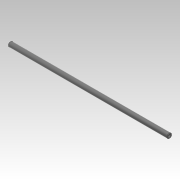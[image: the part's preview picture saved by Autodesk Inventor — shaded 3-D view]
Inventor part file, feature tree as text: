
AUTODESK INVENTOR PART (.ipt)
format: ipt  version: 2020 (Build 240168000, 168)  size: 91,136 bytes
history: native  units: mm
features: revolve x1, chamfer x1, sketch x1
ambient origin geometry x8: Origin, YZ Plane, XZ Plane, XY Plane, X Axis, Y Axis, Z Axis, Center Point
bodies: Solid1 (feature_tree)
feature tree (3):
  revolve  "Revolution1"  [1 undecoded]
  chamfer  "Chamfer1"  Distance=200.0mm
  sketch  "Sketch1"  dims[d0=2.0mm d1=3.0mm d2=200.0mm d3=90.0deg d4=0.5mm d5=2.0mm d6=45.0deg]
note: 1 required parameter value undecoded (feature->parameter linkage not recoverable at this tier; creation-order binding heuristic only, values carry confidence <= 0.55)
